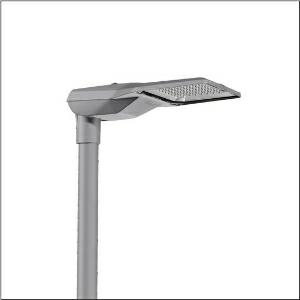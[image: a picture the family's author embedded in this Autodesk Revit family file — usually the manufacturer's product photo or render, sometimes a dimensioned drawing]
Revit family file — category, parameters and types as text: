
# Revit family: streetlight_sl_21_midi___st1_0ab_5xe3m33s08lb_591c
name_source: partatom
category: Lighting Fixtures
units: mm (PartAtom-declared; Revit-internal decimal feet)

## family parameters
Cut with Voids When Loaded = No
Host = Face
Light Source = No
Part Type = Normal
Room Calculation Point = No
Round Connector Dimension = Use Diameter
Shared = No

## types (1)
- --- (1 x LED, 12620 lm, 99.6 W, 3000K)
    Apparent Load = 100 VA
    CIE Flux Codes = 38 73 97 100 100
    Color Rendering = 70
    Color Temperature = 3000K
    Default Elevation = 1800 mm
    Description = Streetlight SL 21 midi, mast luminaire, primary light control with lens, of PMMA, primary optical cover: cover, of toughened safety glass, transparent, light distribution: ST1.0aB, light emission: direct distribution, primary light characteristic: asymmetric, installation type: side-entry, post-top, LED, High Power LED, rated luminous flux: 12.620lm, luminous efficacy: 127lm/W, light colour: 730, colour temperature: 3000K, control gear: D4i, control: flexible luminous flux parameterisation, time-dependent luminous flux control, constant luminous flux control, overheat protection, pre-setting: logarithmic dimming characteristic, mains connection: 230..240V, AC, 50/60Hz, start of lifetime: 100W, end of service life: 102W, reduction: 46W, luminaire housing, of diecast aluminium, powder-coated, Siteco® metallic grey (DB 702S), corrosivity category C5 mid according to DIN EN ISO 12944, please order mast flange separately, inclination adjustable: 0°, 5°, 10°, 15°, sealing non-destructively replaceable, multi-level sealing system, length: 644mm, width: 335mm, height: 110mm, mast flange for spigot size: 42mm (side-entry): 5XC10008XM4, 60/48mm (side-entry/post-top): 5XC10108XM2, 76/60mm (side-entry/post-top): 5XC10108XM1, mounting height: 4..8m, Smart Interface above, protection rating (complete): IP66, insulation class (complete): insulation class II (safety insulation), certification: CE, ENEC, ENEC+, VDE, impact resistance: IK10, permissible operating ambient temperature for outdoor applications: -40..+50°C, standard-compliant lighting for roads and squares, packaging unit: 1 piece

Light Distribution: ST1.0aB
    Height = 111 mm
    Lamp = 1 x LED
    Lamp Light Flux = 12620 lm
    Lamp Power = 99.6 W
    Lamp count = 1
    Length = 644 mm
    Luminous efficacy = 127 lm/W
    Manufacturer = Siteco
    ModVariant = No
    Model = 5XE3M33S08LB
    Number of Poles = 1
    OnlyDefault = Yes
    Power Factor = 1
    Product Name = Streetlight SL 21 midi | ST1.0aB
    Product group = mast luminaire | pylon top
    ProductGroupID = 6100
    Protection Class = Protection class II
    Protection Degree = IP 66
    RLX_Detail_Level = 1
    RLX_Emergency_Light_Flux = 0 lm
    RLX_Emergency_Type = 0
    RLX_Emergency_Type_DB = No
    RlxData = <blob elided: 26825 chars, md5=85efb056>
    Socket = socket
    Standby Power = 0 W
    System Light Flux = 12620 lm
    System Power = 100 W
    Type Comments = factory setting: luminous flux: 100 % | dim-lin: 254 | 1020 mA
    Type Image = l_1004302.jpg
    URL = http://relux.com
    VarID = @adj_030869
    Voltage = 0 V
    Weight = 0.00 kg
    Width = 336 mm

## geometry (parser evidence)
native form markers: Blend x4, Sweep x11
no freeform markers — native parametric forms only
